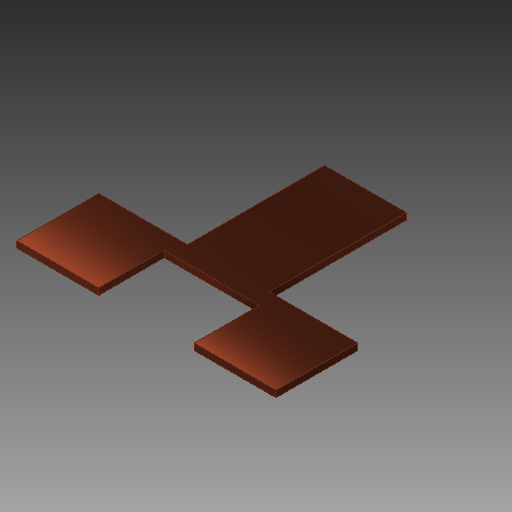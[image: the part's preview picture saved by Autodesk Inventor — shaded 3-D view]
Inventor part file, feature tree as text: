
AUTODESK INVENTOR PART (.ipt)
format: ipt  version: 2019.3 (Build 233278000, 278)  size: 100,864 bytes
history: native  units: mm
features: other x1, extrude x1, sketch x1
ambient origin geometry x8: Origin, YZ Plane, XZ Plane, XY Plane, X Axis, Y Axis, Z Axis, Center Point
bodies: Solid1 (feature_tree)
feature tree (3):
  other  "Housing Box 1.ipt"
  extrude  "Extrusion1"  Depth=2.0mm TaperAngle=0.0deg
  sketch  "Sketch19"  dims[d0=10.0mm d1=2.0mm d2=0.0mm]
